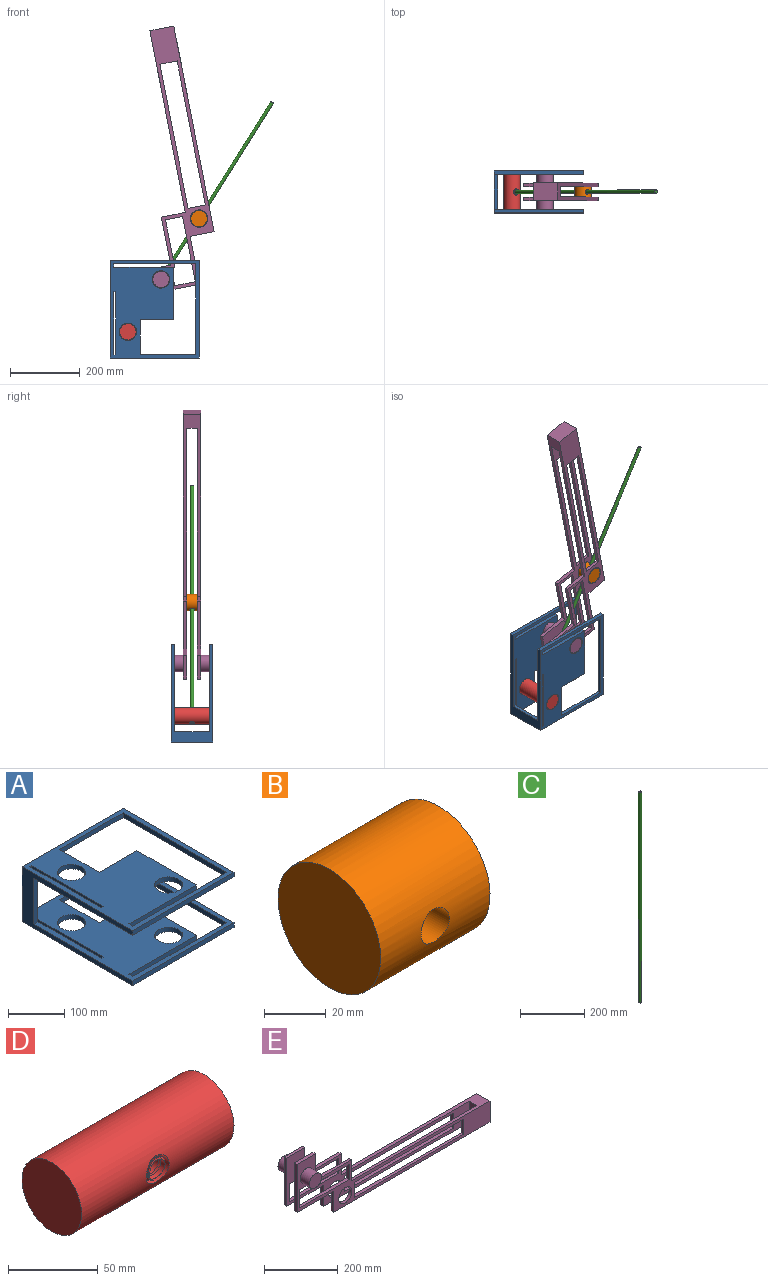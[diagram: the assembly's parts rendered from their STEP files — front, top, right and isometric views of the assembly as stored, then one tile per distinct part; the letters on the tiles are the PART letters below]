
ASSEMBLY  parts=5 mates=5
PART A: 40 faces, bbox 255x280x120 mm
  f0: plane 280x255mm, normal (0,0,1), area 38473mm2, adj f4,f5,f6,f7,f11,f12,f16,f17
  f1: plane 280x255mm, normal (0,0,-1), area 38473mm2, adj f6,f7,f8,f9,f13,f14,f28,f29
  f2: plane 280x255mm, normal (0,0,1), area 38179mm2, adj f6,f7,f8,f9,f10,f13,f14,f15
  f3: plane 280x255mm, normal (0,0,-1), area 38179mm2, adj f4,f5,f6,f7,f10,f11,f12,f15
  f4: plane 255x10mm, normal (0,-1,0), area 2550mm2, adj f0,f3,f5,f7
  f5: plane 280x10mm, normal (1,0,0), area 2800mm2, adj f0,f3,f4,f6
  f6: plane 255x120mm, normal (0,1,0), area 6080mm2, adj f0,f1,f2,f3,f5,f7,f9,f10
  f7: plane 280x120mm, normal (-1,0,0), area 8600mm2, adj f0,f1,f2,f3,f4,f6,f8,f15
  f8: plane 255x10mm, normal (0,-1,0), area 2550mm2, adj f1,f2,f7,f9
  f9: plane 280x10mm, normal (1,0,0), area 2800mm2, adj f1,f2,f6,f8
  f10: plane 100x30mm, normal (1,0,0), area 3000mm2, adj f2,f3,f6,f15
  f11: cylinder r=25mm len=50mm, axis (0,0,1), area 1570.8mm2, adj f0,f3
  f12: cylinder r=25mm len=50mm, axis (0,0,1), area 1570.8mm2, adj f0,f3
  f13: cylinder r=25mm len=50mm, axis (0,0,1), area 1570.8mm2, adj f1,f2
  f14: cylinder r=25mm len=50mm, axis (0,0,1), area 1570.8mm2, adj f1,f2
  f15: plane 100x9.8mm, normal (0,-1,0), area 980mm2, adj f2,f3,f7,f10
  f16: plane 180x10mm, normal (-1,0,0), area 1800mm2, adj f0,f3,f17,f19
  f17: plane 10x5mm, normal (0,1,0), area 50mm2, adj f0,f3,f16,f18
  f18: plane 180x10mm, normal (1,0,0), area 1800mm2, adj f0,f3,f17,f19
  f19: plane 10x5mm, normal (0,-1,0), area 50mm2, adj f0,f3,f16,f18
  f20: plane 10x10mm, normal (1,0,0), area 100mm2, adj f0,f3,f21,f27
  f21: plane 170x10mm, normal (0,-1,0), area 1700mm2, adj f0,f3,f20,f22
  f22: plane 150x10mm, normal (1,0,0), area 1500mm2, adj f0,f3,f21,f23
  f23: plane 95x10mm, normal (0,1,0), area 950mm2, adj f0,f3,f22,f24
  f24: plane 100x10mm, normal (1,0,0), area 1000mm2, adj f0,f3,f23,f25
  f25: plane 160x10mm, normal (0,-1,0), area 1600mm2, adj f0,f3,f24,f26
  f26: plane 260x10mm, normal (-1,0,0), area 2600mm2, adj f0,f3,f25,f27
  f27: plane 235x10mm, normal (0,1,0), area 2350mm2, adj f0,f3,f20,f26
  f28: plane 10x5mm, normal (0,-1,0), area 50mm2, adj f1,f2,f29,f31
  f29: plane 180x10mm, normal (1,0,0), area 1800mm2, adj f1,f2,f28,f30
  f30: plane 10x5mm, normal (0,1,0), area 50mm2, adj f1,f2,f29,f31
  f31: plane 180x10mm, normal (-1,0,0), area 1800mm2, adj f1,f2,f28,f30
  f32: plane 235x10mm, normal (0,1,0), area 2350mm2, adj f1,f2,f33,f39
  f33: plane 260x10mm, normal (-1,0,0), area 2600mm2, adj f1,f2,f32,f34
  f34: plane 160x10mm, normal (0,-1,0), area 1600mm2, adj f1,f2,f33,f35
  f35: plane 100x10mm, normal (1,0,0), area 1000mm2, adj f1,f2,f34,f36
  f36: plane 95x10mm, normal (0,1,0), area 950mm2, adj f1,f2,f35,f37
  f37: plane 150x10mm, normal (1,0,0), area 1500mm2, adj f1,f2,f36,f38
  f38: plane 170x10mm, normal (0,-1,0), area 1700mm2, adj f1,f2,f37,f39
  f39: plane 10x10mm, normal (1,0,0), area 100mm2, adj f1,f2,f32,f38
PART B: 4 faces, bbox 50x47x47 mm
  f0: cylinder r=23.5mm len=50mm, axis (1,0,0), area 7114.4mm2, adj f1,f2,f3
  f1: plane 47x47mm, normal (-1,0,0), area 1734.9mm2, adj f0
  f2: cylinder r=6.5mm len=47mm, axis (0,1,0), area 1882.3mm2, adj f0
  f3: plane 47x47mm, normal (1,0,0), area 1734.9mm2, adj f0
PART C: 3 faces, bbox 10x10x800 mm
  f0: cylinder r=5mm len=800mm, axis (0,0,-1), area 25132.7mm2, adj f1,f2
  f1: plane 10x10mm, normal (0,0,1), area 78.5mm2, adj f0
  f2: plane 10x10mm, normal (0,0,-1), area 78.5mm2, adj f0
PART D: 18 faces, bbox 120x48.7x47 mm
  f0: cylinder r=23.5mm len=120mm, axis (-1,0,0), area 17326.1mm2, adj f1,f11,f12,f13
  f1: cylinder r=6.5mm len=13mm, axis (0,1,0), area 373.7mm2, adj f0,f2,f14,f15,f16
  f2: cylinder r=6.5mm len=13mm, axis (0,1,0), area 132.8mm2, adj f1,f3,f15,f16
  f3: cylinder r=6.5mm len=13mm, axis (0,1,0), area 132.8mm2, adj f2,f4,f15,f16
  f4: cylinder r=6.5mm len=13mm, axis (0,1,0), area 132.8mm2, adj f3,f5,f15,f16
  f5: cylinder r=6.5mm len=13mm, axis (0,1,0), area 132.8mm2, adj f4,f6,f15,f16
  f6: cylinder r=6.5mm len=13mm, axis (0,1,0), area 132.8mm2, adj f5,f7,f15,f16
  f7: cylinder r=6.5mm len=13mm, axis (0,1,0), area 132.8mm2, adj f6,f8,f15,f16
  f8: cylinder r=6.5mm len=13mm, axis (0,1,0), area 129.1mm2, adj f7,f9,f10,f15,f16
  f9: cylinder r=6.5mm len=12.36mm, axis (0,1,0), area 17.2mm2, adj f8,f10,f16
  f10: cylinder r=23.5mm len=13.46mm, axis (-1,0,0), area 23.3mm2, adj f8,f9,f15,f16
  f11: plane 47x47mm, normal (1,0,0), area 1734.9mm2, adj f0
  f12: plane 47x47mm, normal (-1,0,0), area 1734.9mm2, adj f0
  f13: cylinder r=8.98mm len=41.22mm, axis (0,1,0), area 2185.7mm2, adj f0,f14,f17
  f14: plane 6.01x3.66mm, normal (0.6,0,0.8), area 18.2mm2, adj f1,f13,f15,f16,f17
  f15: bspline ~42.41x15.26mm, area 691mm2, adj f1,f2,f3,f4,f5,f6,f7,f8
  f16: bspline ~41.67x17.79mm, area 766.8mm2, adj f1,f2,f3,f4,f5,f6,f7,f8
  f17: bspline ~20.58x19.11mm, area 77mm2, adj f13,f14,f15
PART E: 48 faces, bbox 740x120x230 mm
  f0: plane 740x230mm, normal (0,-1,0), area 28301.6mm2, adj f4,f6,f9,f13,f15,f16,f17,f18
  f1: plane 740x230mm, normal (0,1,0), area 28301.6mm2, adj f5,f7,f8,f9,f10,f11,f12,f14
  f2: plane 700x230mm, normal (0,-1,0), area 27236.5mm2, adj f5,f7,f8,f9,f10,f11,f12,f14
  f3: plane 700x230mm, normal (0,1,0), area 27236.5mm2, adj f4,f6,f9,f13,f15,f16,f18,f19
  f4: plane 70x10mm, normal (-1,0,0), area 700mm2, adj f0,f3,f15,f16
  f5: plane 70x10mm, normal (0,0,1), area 700mm2, adj f1,f2,f12,f14
  f6: plane 160x10mm, normal (-1,0,0), area 1600mm2, adj f0,f3,f13,f15
  f7: plane 140x10mm, normal (0,0,-1), area 1400mm2, adj f1,f2,f8,f14
  f8: plane 70x10mm, normal (-1,0,0), area 700mm2, adj f1,f2,f7,f16
  f9: plane 530x50mm, normal (0,0,1), area 11800mm2, adj f0,f1,f2,f3,f10,f17,f18,f25
  f10: plane 70x10mm, normal (1,0,0), area 700mm2, adj f1,f2,f9,f11
  f11: plane 140x10mm, normal (0,0,1), area 1400mm2, adj f1,f2,f10,f12
  f12: plane 90x10mm, normal (1,0,0), area 900mm2, adj f1,f2,f5,f11
  f13: plane 70x10mm, normal (0,0,1), area 700mm2, adj f0,f3,f6,f20
  f14: plane 160x10mm, normal (-1,0,0), area 1600mm2, adj f1,f2,f5,f7
  f15: plane 140x10mm, normal (0,0,-1), area 1400mm2, adj f0,f3,f4,f6
  f16: plane 600x50mm, normal (0,0,-1), area 13200mm2, adj f0,f1,f2,f3,f4,f8,f17,f25
  f17: plane 70x50mm, normal (1,0,0), area 3500mm2, adj f0,f1,f9,f16
  f18: plane 70x10mm, normal (1,0,0), area 700mm2, adj f0,f3,f9,f19
  f19: plane 140x10mm, normal (0,0,1), area 1400mm2, adj f0,f3,f18,f20
  f20: plane 90x10mm, normal (1,0,0), area 900mm2, adj f0,f3,f13,f19
  f21: cylinder r=23.5mm len=47mm, axis (0,1,0), area 5167.9mm2, adj f0,f22
  f22: plane 47x47mm, normal (0,-1,0), area 1734.9mm2, adj f21
  f23: cylinder r=23.5mm len=47mm, axis (0,-1,0), area 5167.9mm2, adj f1,f24
  f24: plane 47x47mm, normal (0,1,0), area 1734.9mm2, adj f23
  f25: plane 70x30mm, normal (-1,0,0), area 2100mm2, adj f2,f3,f9,f16
  f26: cylinder r=25mm len=50mm, axis (0,-1,0), area 1570.8mm2, adj f0,f3
  f27: cylinder r=25mm len=50mm, axis (0,-1,0), area 1570.8mm2, adj f1,f2
  f28: plane 60x10mm, normal (1,0,0), area 600mm2, adj f0,f3,f29,f33
  f29: plane 50x10mm, normal (0,0,-1), area 500mm2, adj f0,f3,f28,f30
  f30: plane 10x10mm, normal (-1,0,0), area 100mm2, adj f0,f3,f29,f31
  f31: plane 140x10mm, normal (0,0,-1), area 1400mm2, adj f0,f3,f30,f32
  f32: plane 50x10mm, normal (-1,0,0), area 500mm2, adj f0,f3,f31,f33
  f33: plane 190x10mm, normal (0,0,1), area 1900mm2, adj f0,f3,f28,f32
  f34: plane 50x10mm, normal (-1,0,0), area 500mm2, adj f0,f3,f35,f37
  f35: plane 420x10mm, normal (0,0,1), area 4200mm2, adj f0,f3,f34,f36
  f36: plane 50x10mm, normal (1,0,0), area 500mm2, adj f0,f3,f35,f37
  f37: plane 420x10mm, normal (0,0,-1), area 4200mm2, adj f0,f3,f34,f36
  f38: plane 190x10mm, normal (0,0,1), area 1900mm2, adj f1,f2,f39,f43
  f39: plane 50x10mm, normal (-1,0,0), area 500mm2, adj f1,f2,f38,f40
  f40: plane 140x10mm, normal (0,0,-1), area 1400mm2, adj f1,f2,f39,f41
  f41: plane 10x10mm, normal (-1,0,0), area 100mm2, adj f1,f2,f40,f42
  f42: plane 50x10mm, normal (0,0,-1), area 500mm2, adj f1,f2,f41,f43
  f43: plane 60x10mm, normal (1,0,0), area 600mm2, adj f1,f2,f38,f42
  f44: plane 420x10mm, normal (0,0,-1), area 4200mm2, adj f1,f2,f45,f47
  f45: plane 50x10mm, normal (1,0,0), area 500mm2, adj f1,f2,f44,f46
  f46: plane 420x10mm, normal (0,0,1), area 4200mm2, adj f1,f2,f45,f47
  f47: plane 50x10mm, normal (-1,0,0), area 500mm2, adj f1,f2,f44,f46
PLACE A rot(axis=(-1,0,0),90deg) t=(116.92,-197.24,850.39)mm fixed
PLACE B rot(axis=(0.66,0.66,0.36),140deg) t=(399.55,-162.24,1128.39)mm
PLACE C rot(axis=(-0.96,0,0.28),180deg) t=(579.89,-137.24,1302.63)mm
PLACE D rot(axis=(-0.44,-0.44,0.79),103.5deg) t=(145.42,-187.24,517.18)mm
PLACE E rot(axis=(0,-1,0),101.1deg) t=(440.39,-112.24,794.61)mm
MATE slider C.f0 <-> B.f2  axis (0.53,0,0.85) through (367.08,-137.24,963.93)mm
MATE revolute C.f0 <-> D.f1  axis (-0.53,0,-0.85) through (154.26,-137.24,625.24)mm
MATE revolute E.f21 <-> A.f12  axis (0,-1,0) through (261.92,-197.24,795.39)mm
MATE revolute E.f26 <-> B.f0  axis (0,-1,0) through (370.55,-162.24,969.46)mm
MATE revolute D.f0 <-> A.f11  axis (0,-1,0) through (166.92,-197.24,645.39)mm
